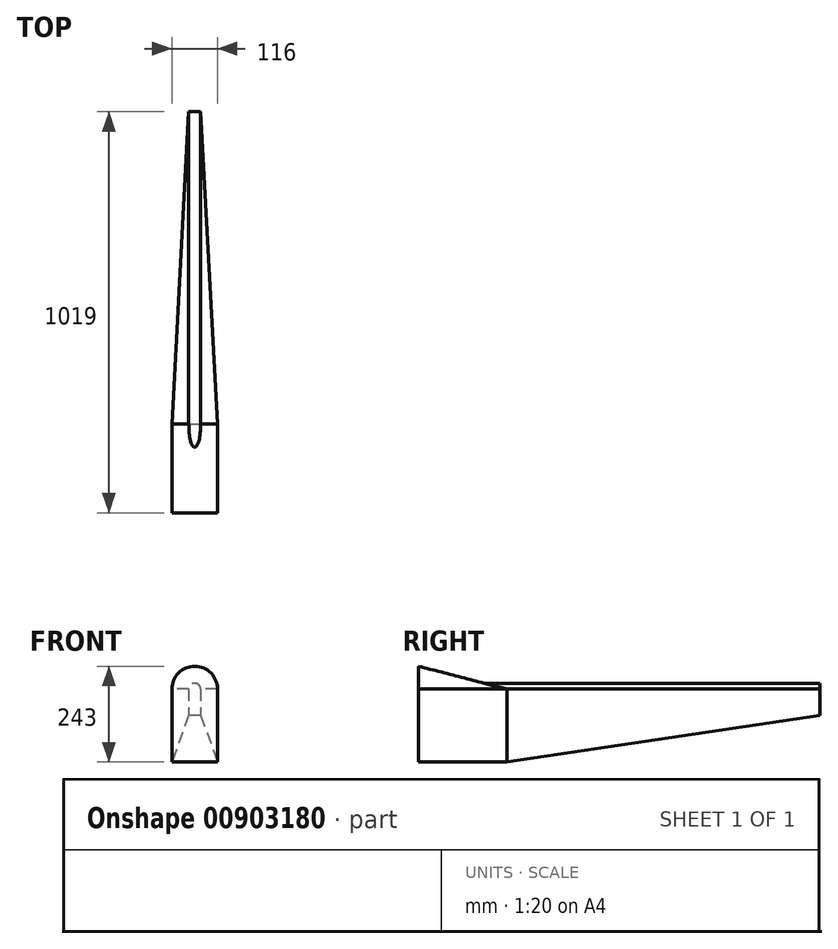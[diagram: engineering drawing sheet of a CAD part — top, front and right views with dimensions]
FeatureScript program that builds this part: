
annotation { "Feature Type Name" : "Feature", "Feature Type Description" : "" }
export const myFeature = defineFeature(function(context is Context, id is Id, definition is map)
    precondition{}
    {
        {
            var Q0;
            Q0=qCreatedBy(makeId("Front.planeOp"),FACE);
            var sketch = newSketch(context, id + "F0", { "sketchPlane" : qUnion([Q0])});
            skLineSegment(sketch, "E0.bottom", {"start": v(-58, 92.5) * mm, "end": v(58, 92.5) * mm});
            skLineSegment(sketch, "E0.top", {"start": v(-58, -92.5) * mm, "end": v(58, -92.5) * mm});
            skLineSegment(sketch, "E0.left", {"start": v(-58, 92.5) * mm, "end": v(-58, -92.5) * mm});
            skLineSegment(sketch, "E0.right", {"start": v(58, 92.5) * mm, "end": v(58, -92.5) * mm});
            skArc(sketch, "E1", {"start": v(58, 92.5) * mm, "mid": v(0, 150.5) * mm, "end": v(-58, 92.5) * mm});
            skSolve(sketch);
        }
        {
            var Q0;
            Q0=makeQuery(id+"F0.imprint","IMPRINT",FACE,{"disambiguationData":[TD([[makeQuery(id+"F0.imprint","IMPRINT",EDGE,{"derivedFrom":sQuery(id+"F0.wireOp",EDGE,"E0.bottom")}),1.0]])]});
            cPlane(context, id + "F1", {"entities" : qUnion([Q0]), "cplaneType" : CPlaneType.OFFSET, "offset" : 1019 * mm, "oppositeDirection" : true, "width" : 150 * mm, "height" : 150 * mm});
        }
        {
            var Q0;
            Q0=makeQuery(id+"F0.imprint","IMPRINT",FACE,{"disambiguationData":[TD([[makeQuery(id+"F0.imprint","IMPRINT",EDGE,{"derivedFrom":sQuery(id+"F0.wireOp",EDGE,"E0.bottom")}),-1.0]])]});
            cPlane(context, id + "F2", {"entities" : qUnion([Q0]), "cplaneType" : CPlaneType.OFFSET, "offset" : 225 * mm, "oppositeDirection" : true, "width" : 150 * mm, "height" : 150 * mm});
        }
        {
            var Q0;
            Q0=qCreatedBy(id+"F2.planeOp",FACE);
            var sketch = newSketch(context, id + "F3", { "sketchPlane" : qUnion([Q0])});
            skLineSegment(sketch, "E2.0.0", {"start": v(-58, 92.5) * mm, "end": v(-58, -92.5) * mm});
            skLineSegment(sketch, "E2.0.1", {"start": v(-58, -92.5) * mm, "end": v(58, -92.5) * mm});
            skLineSegment(sketch, "E2.0.2", {"start": v(58, -92.5) * mm, "end": v(58, 92.5) * mm});
            skLineSegment(sketch, "E2.0.3", {"start": v(58, 92.5) * mm, "end": v(-58, 92.5) * mm});
            skSolve(sketch);
        }
        {
            var Q0;
            Q0 = qSketchRegion(id + "F0", true);
            var Q1;
            Q1=makeQuery(id+"F3.imprint","IMPRINT",FACE,{"disambiguationData":[TD([[makeQuery(id+"F3.imprint","IMPRINT",EDGE,{"derivedFrom":sQuery(id+"F3.wireOp",EDGE,"E2.0.0")}),1.0]])]});
            loft(context, id + "F4", {"sheetProfilesArray" : [{ "sheetProfileEntities" : qUnion([Q0]) }, { "sheetProfileEntities" : qUnion([Q1]) }]});
        }
        {
            var Q0;
            Q0=qCreatedBy(id+"F1.planeOp",FACE);
            var sketch = newSketch(context, id + "F5", { "sketchPlane" : qUnion([Q0])});
            skLineSegment(sketch, "E3.0.0", {"start": v(58, 92.5) * mm, "end": v(58, -92.5) * mm});
            skLineSegment(sketch, "E3.0.1", {"start": v(58, -92.5) * mm, "end": v(-58, -92.5) * mm});
            skLineSegment(sketch, "E3.0.2", {"start": v(-58, -92.5) * mm, "end": v(-58, 92.5) * mm});
            skLineSegment(sketch, "E3.0.3", {"start": v(-58, 92.5) * mm, "end": v(58, 92.5) * mm});
            skLineSegment(sketch, "E4.bottom", {"start": v(15, 92.5) * mm, "end": v(-15, 92.5) * mm});
            skLineSegment(sketch, "E4.top", {"start": v(15, 25.5) * mm, "end": v(-15, 25.5) * mm});
            skLineSegment(sketch, "E4.left", {"start": v(15, 92.5) * mm, "end": v(15, 25.5) * mm});
            skLineSegment(sketch, "E4.right", {"start": v(-15, 92.5) * mm, "end": v(-15, 25.5) * mm});
            skSolve(sketch);
        }
        {
            var Q1;
            Q1=makeQuery(id+"F5.imprint","IMPRINT",FACE,{"disambiguationData":[TD([[makeQuery(id+"F5.imprint","IMPRINT",EDGE,{"derivedFrom":sQuery(id+"F5.wireOp",EDGE,"E4.top")}),-1.0]])]});
            var Q2;
            Q2=makeQuery(id+"F4.opLoft","CAP_FACE",FACE,{"disambiguationData":[OSD([makeQuery(id+"F3.imprint","IMPRINT",FACE,{"disambiguationData":[TD([[makeQuery(id+"F3.imprint","IMPRINT",EDGE,{"derivedFrom":sQuery(id+"F3.wireOp",EDGE,"E2.0.0")}),1.0]])]})])],"isStart":true});
            loft(context, id + "F6", {"operationType" : NewBodyOperationType.ADD, "sheetProfilesArray" : [{ "sheetProfileEntities" : qUnion([Q1]) }, { "sheetProfileEntities" : qUnion([Q2]) }]});
        }
        {
            var Q0;
            Q0=qCreatedBy(id+"F1.planeOp",FACE);
            var sketch = newSketch(context, id + "F7", { "sketchPlane" : qUnion([Q0])});
            skLineSegment(sketch, "E5.0", {"start": v(15, 92.5) * mm, "end": v(-15, 92.5) * mm});
            skArc(sketch, "E6", {"start": v(15, 92.5) * mm, "mid": v(0, 107.5) * mm, "end": v(-15, 92.5) * mm});
            skSolve(sketch);
        }
        {
            var Q0;
            Q0=makeQuery(id+"F7.imprint","IMPRINT",FACE,{"disambiguationData":[TD([[makeQuery(id+"F7.imprint","IMPRINT",EDGE,{"derivedFrom":sQuery(id+"F7.wireOp",EDGE,"E5.0")}),-1.0]])]});
            var Q1;
            Q1=makeQuery(id+"F4.opLoft","CAP_FACE",FACE,{"disambiguationData":[OSD([makeQuery(id+"F0.imprint","IMPRINT",FACE,{"disambiguationData":[TD([[makeQuery(id+"F0.imprint","IMPRINT",EDGE,{"derivedFrom":sQuery(id+"F0.wireOp",EDGE,"E0.bottom")}),1.0]])]})])],"isStart":true});
            extrude(context, id + "F8", {"entities" : qUnion([Q0]), "operationType" : NewBodyOperationType.ADD, "endBound" : BoundingType.UP_TO_SURFACE, "depth" : 25 * mm, "endBoundEntityFace" : qUnion([Q1]), "offsetDistance" : 25 * mm});
        }
    });
